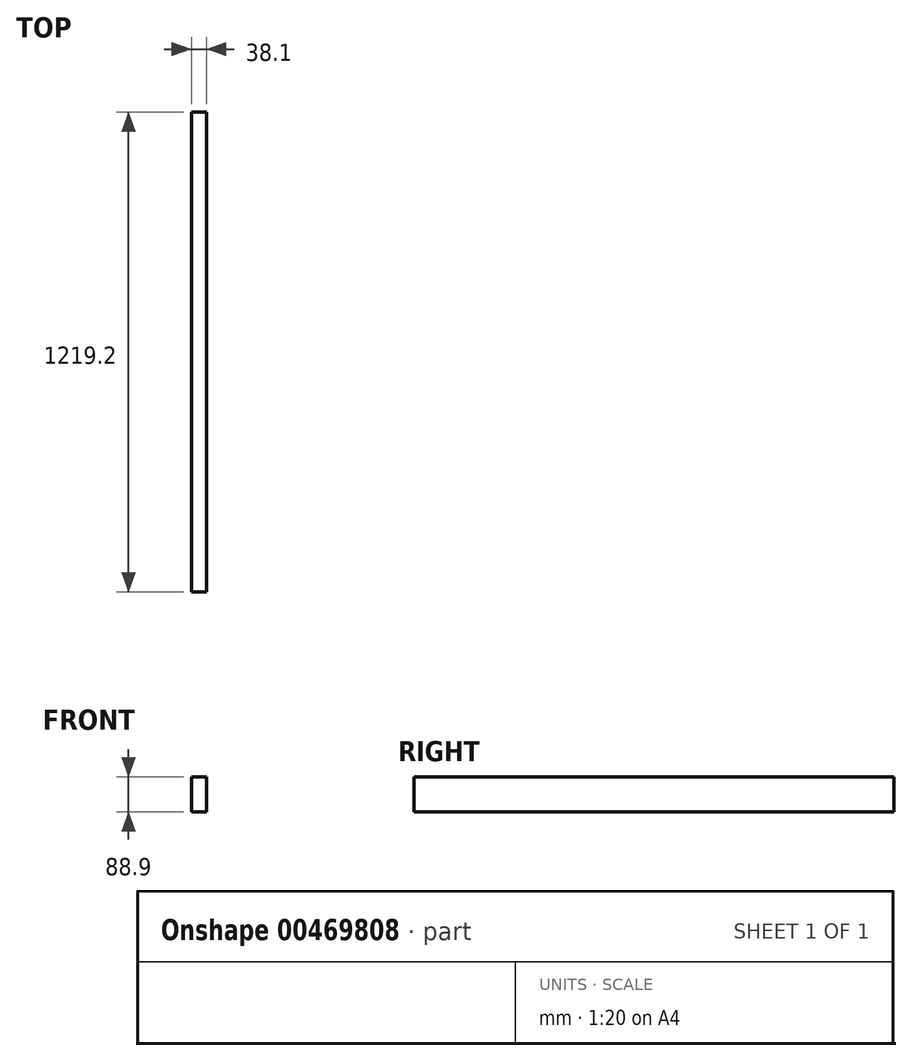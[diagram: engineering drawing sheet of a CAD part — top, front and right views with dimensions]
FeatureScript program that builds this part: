
annotation { "Feature Type Name" : "Feature", "Feature Type Description" : "" }
export const myFeature = defineFeature(function(context is Context, id is Id, definition is map)
    precondition{}
    {
        {
            var Q0;
            Q0=qCreatedBy(makeId("Front.planeOp"),FACE);
            var sketch = newSketch(context, id + "F0", { "sketchPlane" : qUnion([Q0])});
            skLineSegment(sketch, "E0.bottom", {"start": v(19.05, 44.45) * mm, "end": v(-19.05, 44.45) * mm});
            skLineSegment(sketch, "E0.top", {"start": v(19.05, -44.45) * mm, "end": v(-19.05, -44.45) * mm});
            skLineSegment(sketch, "E0.left", {"start": v(19.05, 44.45) * mm, "end": v(19.05, -44.45) * mm});
            skLineSegment(sketch, "E0.right", {"start": v(-19.05, 44.45) * mm, "end": v(-19.05, -44.45) * mm});
            skPoint(sketch, "E0.middle", {"position": v(0, 0) * mm});
            skSolve(sketch);
        }
        {
            var Q0;
            Q0=qSketchRegion(id+"F0",true);
            extrude(context, id + "F1", {"entities" : qUnion([Q0]), "oppositeDirection" : true, "depth" : 1219.2 * mm});
        }
    });
